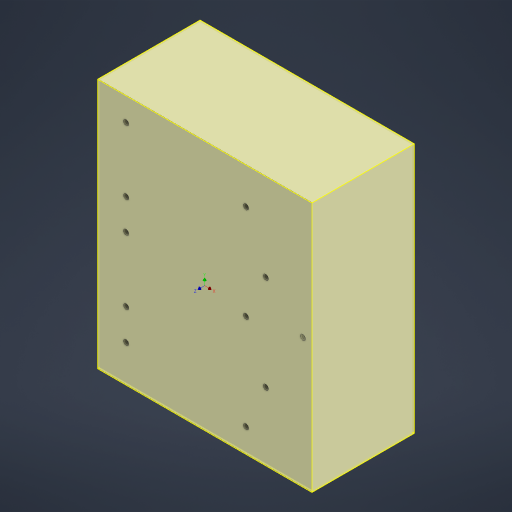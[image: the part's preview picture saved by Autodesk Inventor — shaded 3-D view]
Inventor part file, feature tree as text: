
AUTODESK INVENTOR PART (.ipt)
format: ipt  version: 2024.2 (Build 282272000, 272)  size: 548,864 bytes
history: native  units: in
note: dims shown in document units (in); Inventor stores cm internally (conversion verified against a paired STEP export)
features: other x3, sketch x2, plane x1, extrude x1, hole x1
ambient origin geometry x8: Origin, YZ Plane, XZ Plane, XY Plane, X Axis, Y Axis, Z Axis, Center Point
bodies: Solid2 (feature_tree), Solid1 (feature_tree)
feature tree (8):
  other  "HV servo drive v1_PCB.ipt"
  sketch  "Sketch1"  dims[d0=0.3937in d1=3.42in]
  plane  "Work Plane1"
  extrude  "Extrusion1"  Depth=3.42in
  hole  "Hole1"  [1 undecoded]
  other  "Solid1::HV servo drive v1_PCB.ipt"
  other  "TaggingFeature1"
  sketch  "Sketch2"  dims[d2=4.0in d3=3.47in d4=0.02in d5=0.25in d6=1.63in d7=0.0in d8=0.0849in d9=0.224in d10=0.119in d11=0.25in d12=0.5635in d13=0.28in d14=0.8108in]
note: 1 required parameter value undecoded (feature->parameter linkage not recoverable at this tier; creation-order binding heuristic only, values carry confidence <= 0.55)
